# Revit family: FU_Table_Sandler_Essens_9-2
name_source: partatom
category: Furniture
units: mm (PartAtom-declared; Revit-internal decimal feet)

## family parameters
Always vertical = Yes
Cut with Voids When Loaded = No
OmniClass Number = 23.40.20.00
OmniClass Title = General Furniture and Specialties
Room Calculation Point = No
Shared = No
Work Plane-Based = No

## types (1)
- Essens 9.2
    Base Depth = 364 mm  [stored 1.19423 ft]
    Base Finish = PE1 - G49 Anthracite
    Base Width = 364 mm  [stored 1.19423 ft]
    Default Elevation = 0 mm  [stored 0 ft]
    Depth = 480 mm  [stored 1.5748 ft]
    Height = 1085 mm  [stored 3.55971 ft]
    Section Depth = 180 mm  [stored 0.590551 ft]
    Section Width = 180 mm  [stored 0.590551 ft]
    Width = 480 mm  [stored 1.5748 ft]

note: [stored X ft] marks values corroborated as IEEE doubles in the binary element streams (Revit-internal decimal feet)

## geometry (parser evidence)
native form markers: Sweep x2
no freeform markers — native parametric forms only
